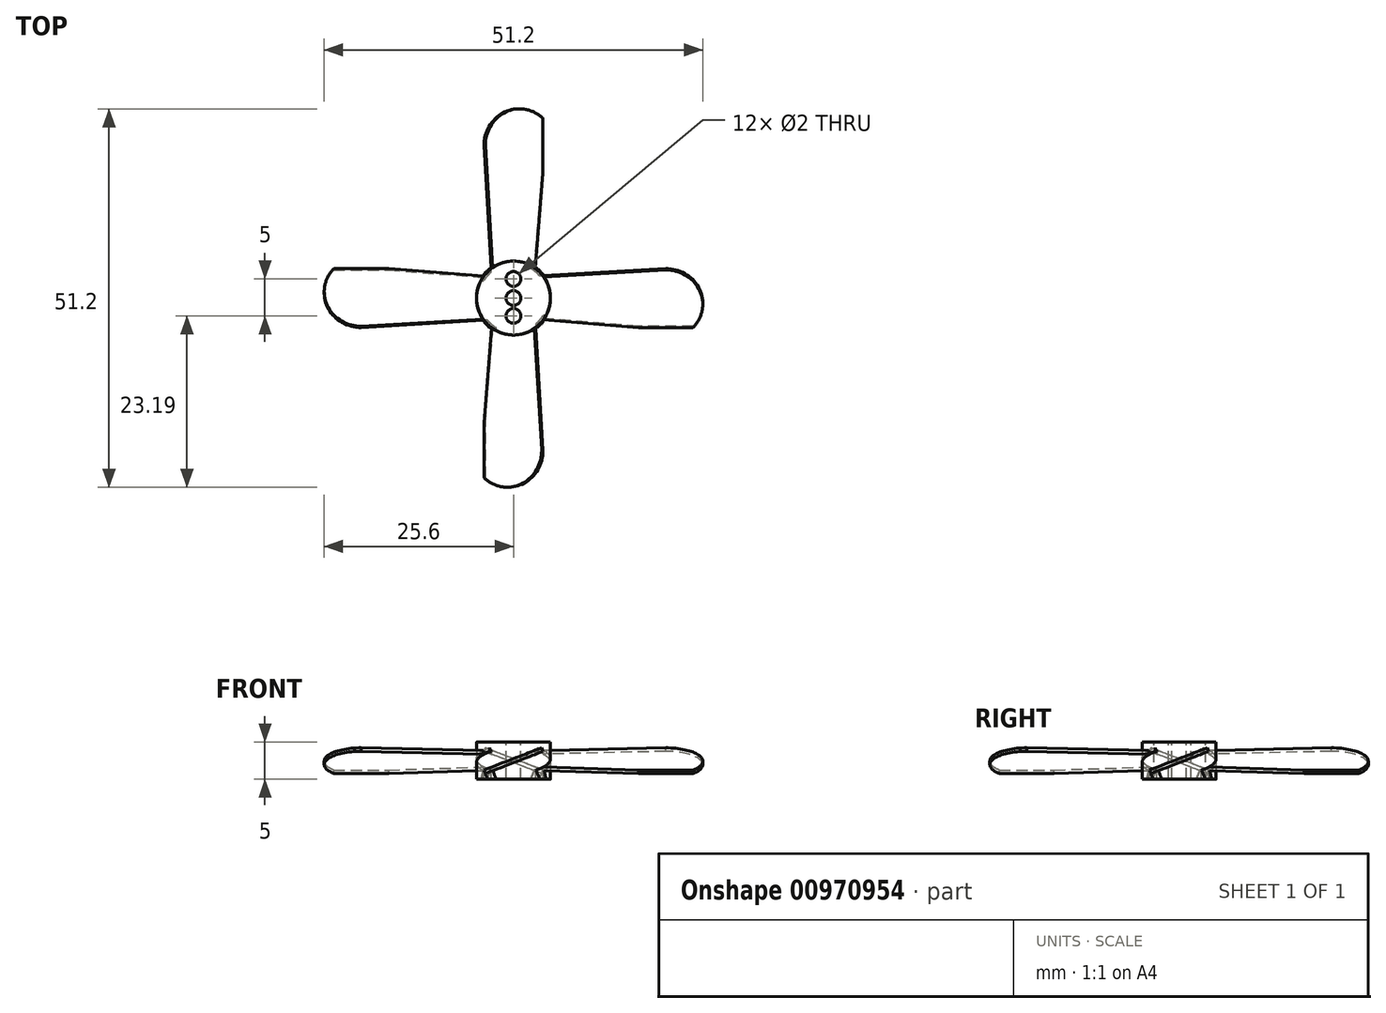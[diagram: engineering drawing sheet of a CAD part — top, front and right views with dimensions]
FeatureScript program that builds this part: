
annotation { "Feature Type Name" : "Feature", "Feature Type Description" : "" }
export const myFeature = defineFeature(function(context is Context, id is Id, definition is map)
    precondition{}
    {
        {
            var Q0;
            Q0=qCreatedBy(makeId("Top.planeOp"),FACE);
            var sketch = newSketch(context, id + "F0", { "sketchPlane" : qUnion([Q0])});
            skCircle(sketch, "E0", {"center": v(0, 0) * mm, "radius": 5 * mm});
            skSolve(sketch);
        }
        {
            var Q0;
            Q0=makeQuery(id+"F0.imprint","IMPRINT",FACE,{"disambiguationData":[TD([[makeQuery(id+"F0.imprint","IMPRINT",EDGE,{"derivedFrom":sQuery(id+"F0.wireOp",EDGE,"E0")}),1.0]])]});
            extrude(context, id + "F1", {"entities" : qUnion([Q0]), "depth" : 5 * mm, "offsetDistance" : 25 * mm});
        }
        {
            var Q0;
            Q0=qCreatedBy(makeId("Right.planeOp"),FACE);
            var sketch = newSketch(context, id + "F2", { "sketchPlane" : qUnion([Q0])});
            skLineSegment(sketch, "E1", {"start": v(0, 0) * mm, "end": v(0, 6.66) * mm, "construction": true});
            skLineSegment(sketch, "E2", {"start": v(0, 0) * mm, "end": v(8.16, 0) * mm, "construction": true});
            skLineSegment(sketch, "E3", {"start": v(-3.9, 1) * mm, "end": v(3.9, 4) * mm, "construction": true});
            skLineSegment(sketch, "E4.0", {"start": v(-3.99, 1.23) * mm, "end": v(3.81, 4.23) * mm});
            skLineSegment(sketch, "E5.0", {"start": v(-3.81, 0.77) * mm, "end": v(3.99, 3.77) * mm});
            skLineSegment(sketch, "E6", {"start": v(3.81, 4.23) * mm, "end": v(3.99, 3.77) * mm});
            skLineSegment(sketch, "E7", {"start": v(-3.81, 0.77) * mm, "end": v(-3.99, 1.23) * mm});
            skPoint(sketch, "E8.visualSharp", {"position": v(3.81, 4.23) * mm});
            skPoint(sketch, "E9.visualSharp", {"position": v(3.99, 3.77) * mm});
            skPoint(sketch, "E10.visualSharp", {"position": v(-3.81, 0.77) * mm});
            skPoint(sketch, "E11.visualSharp", {"position": v(-3.99, 1.23) * mm});
            skLineSegment(sketch, "E12.MirrorCS", {"start": v(3.99, 1.23) * mm, "end": v(-3.81, 4.23) * mm});
            skLineSegment(sketch, "E13.MirrorCS", {"start": v(3.81, 0.77) * mm, "end": v(-3.99, 3.77) * mm});
            skLineSegment(sketch, "E14.MirrorCS", {"start": v(3.9, 1) * mm, "end": v(-3.9, 4) * mm, "construction": true});
            skLineSegment(sketch, "E15.MirrorCS", {"start": v(-3.81, 4.23) * mm, "end": v(-3.99, 3.77) * mm});
            skLineSegment(sketch, "E16.MirrorCS", {"start": v(3.81, 0.77) * mm, "end": v(3.99, 1.23) * mm});
            skSolve(sketch);
        }
        {
            var Q0;
            {var subQ0=sQuery(id+"F2.wireOp",EDGE,"E13.MirrorCS");var subQ1=sQuery(id+"F2.wireOp",EDGE,"E4.0");var subQ2=makeQuery(id+"F2.imprint","INTERSECT",VERTEX,{"derivedFrom":[subQ1,subQ0]});Q0=makeQuery(id+"F2.imprint","IMPRINT",FACE,{"disambiguationData":[TD([[makeQuery(id+"F2.imprint","IMPRINT",EDGE,{"disambiguationData":[TD([[subQ2,-1.0]])],"derivedFrom":subQ1}),-1.0]])]});}
            var Q1;
            {var subQ0=sQuery(id+"F2.wireOp",EDGE,"E6");Q1=makeQuery(id+"F2.imprint","IMPRINT",FACE,{"disambiguationData":[TD([[makeQuery(id+"F2.imprint","IMPRINT",EDGE,{"derivedFrom":subQ0}),-1.0]])]});}
            var Q2;
            {var subQ0=sQuery(id+"F2.wireOp",EDGE,"E7");Q2=makeQuery(id+"F2.imprint","IMPRINT",FACE,{"disambiguationData":[TD([[makeQuery(id+"F2.imprint","IMPRINT",EDGE,{"derivedFrom":subQ0}),-1.0]])]});}
            extrude(context, id + "F3", {"entities" : qUnion([Q0, Q1, Q2]), "operationType" : NewBodyOperationType.ADD, "depth" : 25.6 * mm, "offsetDistance" : 25 * mm});
        }
        {
            var Q0;
            Q0=makeQuery(id+"F3.opExtrude","SWEPT_FACE",FACE,{"disambiguationData":[OSD([sQuery(id+"F2.wireOp",EDGE,"E4.0")])]});
            var sketch = newSketch(context, id + "F4", { "sketchPlane" : qUnion([Q0])});
            skCircle(sketch, "E17", {"center": v(20.6, 0.08) * mm, "radius": 5 * mm});
            skLineSegment(sketch, "E18", {"start": v(20.6, 5.08) * mm, "end": v(0, 3.78) * mm});
            skLineSegment(sketch, "E19", {"start": v(16.9, -3.28) * mm, "end": v(0, -1.82) * mm});
            skSolve(sketch);
        }
        {
            var Q0;
            {var subQ0=sQuery(id+"F4.wireOp",EDGE,"E18");var subQ1=sQuery(id+"F4.wireOp",EDGE,"E17");var subQ5=makeQuery(id+"F4.imprint","INTERSECT",VERTEX,{"derivedFrom":[subQ1,subQ0]});Q0=makeQuery(id+"F4.imprint","IMPRINT",FACE,{"disambiguationData":[TD([[makeQuery(id+"F4.imprint","IMPRINT",EDGE,{"disambiguationData":[TD([[subQ5,-1.0]])],"derivedFrom":subQ0}),-1.0]])]});}
            var Q1;
            {var subQ0=sQuery(id+"F4.wireOp",EDGE,"E17");var subQ1=sQuery(id+"F2.wireOp",EDGE,"E4.0");var subQ4=makeQuery(id+"F3.opExtrude","CAP_EDGE",EDGE,{"disambiguationData":[OSD([subQ1])],"isStart":false});var subQ5=makeQuery(id+"F4.imprint","INTERSECT",VERTEX,{"derivedFrom":[subQ4,subQ0]});Q1=makeQuery(id+"F4.imprint","IMPRINT",FACE,{"disambiguationData":[TD([[makeQuery(id+"F4.imprint","IMPRINT",EDGE,{"disambiguationData":[TD([[subQ5,-1.0]])],"derivedFrom":subQ4}),1.0]])]});}
            var Q2;
            {var subQ0=sQuery(id+"F4.wireOp",EDGE,"E18");var subQ1=sQuery(id+"F4.wireOp",EDGE,"E17");var subQ3=makeQuery(id+"F4.imprint","INTERSECT",VERTEX,{"derivedFrom":[subQ1,subQ0]});Q2=makeQuery(id+"F4.imprint","IMPRINT",FACE,{"disambiguationData":[TD([[makeQuery(id+"F4.imprint","IMPRINT",EDGE,{"disambiguationData":[TD([[subQ3,1.0]])],"derivedFrom":subQ1}),1.0]])]});}
            var Q3;
            {var subQ0=sQuery(id+"F4.wireOp",EDGE,"E17");var subQ1=makeQuery(id+"F3.opExtrude","SWEPT_EDGE",EDGE,{"disambiguationData":[OSD([sQuery(id+"F2.wireOp",EDGE,"E4.0"),sQuery(id+"F2.wireOp",EDGE,"E7")])]});var subQ3=makeQuery(id+"F4.imprint","INTERSECT",VERTEX,{"derivedFrom":[subQ1,subQ0]});Q3=makeQuery(id+"F4.imprint","IMPRINT",FACE,{"disambiguationData":[TD([[makeQuery(id+"F4.imprint","IMPRINT",EDGE,{"disambiguationData":[TD([[subQ3,1.0]])],"derivedFrom":subQ0}),1.0]])]});}
            var Q4;
            {var subQ0=sQuery(id+"F4.wireOp",EDGE,"E17");var subQ1=sQuery(id+"F2.wireOp",EDGE,"E4.0");var subQ2=makeQuery(id+"F3.opExtrude","CAP_EDGE",EDGE,{"disambiguationData":[OSD([subQ1])],"isStart":false});var subQ3=makeQuery(id+"F4.imprint","INTERSECT",VERTEX,{"derivedFrom":[subQ2,subQ0]});Q4=makeQuery(id+"F4.imprint","IMPRINT",FACE,{"disambiguationData":[TD([[makeQuery(id+"F4.imprint","IMPRINT",EDGE,{"disambiguationData":[TD([[subQ3,1.0]])],"derivedFrom":subQ0}),-1.0]])]});}
            var Q5;
            {var subQ0=sQuery(id+"F4.wireOp",EDGE,"E19");var subQ1=sQuery(id+"F2.wireOp",EDGE,"E4.0");var subQ4=makeQuery(id+"F3.boolean.opBoolean","INTERSECT",EDGE,{"derivedFrom":[makeQuery(id+"F1.opExtrude","SWEPT_FACE",FACE,{"disambiguationData":[OSD([sQuery(id+"F0.wireOp",EDGE,"E0")])]}),makeQuery(id+"F3.opExtrude","SWEPT_FACE",FACE,{"disambiguationData":[OSD([subQ1])]})]});var subQ5=makeQuery(id+"F4.imprint","INTERSECT",VERTEX,{"derivedFrom":[subQ4,subQ0]});Q5=makeQuery(id+"F4.imprint","IMPRINT",FACE,{"disambiguationData":[TD([[makeQuery(id+"F4.imprint","IMPRINT",EDGE,{"disambiguationData":[TD([[subQ5,1.0]])],"derivedFrom":subQ0}),1.0]])]});}
            extrude(context, id + "F5", {"entities" : qUnion([Q0, Q1, Q2, Q3, Q4, Q5]), "operationType" : NewBodyOperationType.REMOVE, "oppositeDirection" : true, "depth" : 25 * mm, "offsetDistance" : 25 * mm});
        }
        {
            var Q0;
            Q0=makeQuery(id+"F1.opExtrude","SWEPT_BODY",BODY,{"disambiguationData":[OSD([sQuery(id+"F0.wireOp",EDGE,"E0")])]});
            var Q1;
            Q1=sQuery(id+"F2.wireOp",EDGE,"E1");
            circularPattern(context, id + "F6", {"entities" : qUnion([Q0]), "axis" : qUnion([Q1]), "angle" : 360 * degree, "instanceCount" : 4, "equalSpace" : true});
        }
        {
            var Q0;
            Q0=makeQuery(id+"F1.opExtrude","CAP_FACE",FACE,{"disambiguationData":[OSD([sQuery(id+"F0.wireOp",EDGE,"E0")])],"isStart":false});
            var sketch = newSketch(context, id + "F7", { "sketchPlane" : qUnion([Q0])});
            skCircle(sketch, "E20", {"center": v(0, 0) * mm, "radius": 1 * mm});
            skCircle(sketch, "E21", {"center": v(0, 2.59) * mm, "radius": 1 * mm});
            skCircle(sketch, "E22", {"center": v(0, -2.41) * mm, "radius": 1 * mm});
            skSolve(sketch);
        }
        {
            var Q0;
            Q0=makeQuery(id+"F7.imprint","IMPRINT",FACE,{"disambiguationData":[TD([[makeQuery(id+"F7.imprint","IMPRINT",EDGE,{"derivedFrom":sQuery(id+"F7.wireOp",EDGE,"E20")}),1.0]])]});
            var Q1;
            Q1=makeQuery(id+"F7.imprint","IMPRINT",FACE,{"disambiguationData":[TD([[makeQuery(id+"F7.imprint","IMPRINT",EDGE,{"derivedFrom":sQuery(id+"F7.wireOp",EDGE,"E21")}),1.0]])]});
            var Q2;
            Q2=makeQuery(id+"F7.imprint","IMPRINT",FACE,{"disambiguationData":[TD([[makeQuery(id+"F7.imprint","IMPRINT",EDGE,{"derivedFrom":sQuery(id+"F7.wireOp",EDGE,"E22")}),1.0]])]});
            extrude(context, id + "F8", {"entities" : qUnion([Q0, Q1, Q2]), "operationType" : NewBodyOperationType.REMOVE, "oppositeDirection" : true, "depth" : 25 * mm, "offsetDistance" : 25 * mm});
        }
    });
